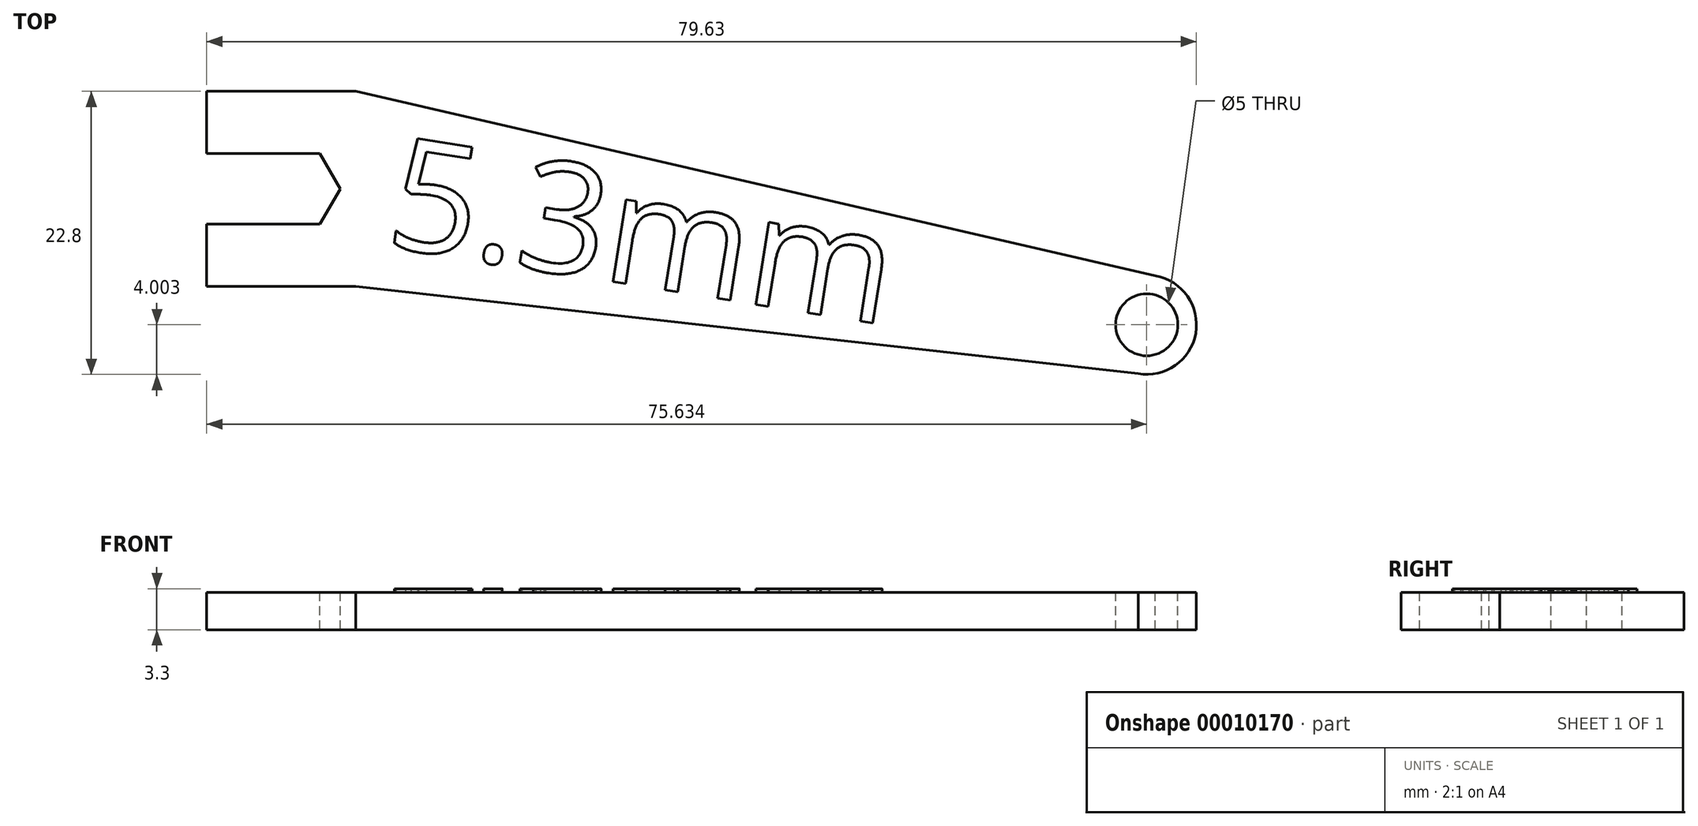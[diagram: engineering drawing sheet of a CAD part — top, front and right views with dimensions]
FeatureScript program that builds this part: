
annotation { "Feature Type Name" : "Feature", "Feature Type Description" : "" }
export const myFeature = defineFeature(function(context is Context, id is Id, definition is map)
    precondition{}
    {
        {
            var Q0;
            Q0=qCreatedBy(makeId("Top.planeOp"),FACE);
            var sketch = newSketch(context, id + "F0", { "sketchPlane" : qUnion([Q0])});
            skCircle(sketch, "E0.cCircle", {"center": v(-19.18, 8.62) * mm, "radius": 2.85 * mm, "construction": true});
            skLineSegment(sketch, "E0.0", {"start": v(-15.89, 8.62) * mm, "end": v(-17.53, 5.77) * mm});
            skLineSegment(sketch, "E0.1", {"start": v(-17.53, 5.77) * mm, "end": v(-20.82, 5.77) * mm});
            skLineSegment(sketch, "E0.2", {"start": v(-20.82, 5.77) * mm, "end": v(-22.47, 8.62) * mm, "construction": true});
            skLineSegment(sketch, "E0.3", {"start": v(-22.47, 8.62) * mm, "end": v(-20.82, 11.47) * mm, "construction": true});
            skLineSegment(sketch, "E0.4", {"start": v(-20.82, 11.47) * mm, "end": v(-17.53, 11.47) * mm});
            skLineSegment(sketch, "E0.5", {"start": v(-17.53, 11.47) * mm, "end": v(-15.89, 8.62) * mm});
            skPoint(sketch, "E0.0.midPoint", {"position": v(-16.7, 7.2) * mm});
            skCircle(sketch, "E1.cCircle", {"center": v(-19.18, 8.62) * mm, "radius": 7.85 * mm, "construction": true});
            skLineSegment(sketch, "E1.0", {"start": v(-14.64, 16.47) * mm, "end": v(-10.11, 8.62) * mm, "construction": true});
            skLineSegment(sketch, "E1.1", {"start": v(-10.11, 8.62) * mm, "end": v(-14.64, 0.77) * mm, "construction": true});
            skLineSegment(sketch, "E1.2", {"start": v(-14.64, 0.77) * mm, "end": v(-23.54, 0.77) * mm});
            skLineSegment(sketch, "E1.3", {"start": v(-23.54, 0.77) * mm, "end": v(-26.65, 5.77) * mm, "construction": true});
            skLineSegment(sketch, "E1.4", {"start": v(-26.65, 11.47) * mm, "end": v(-23.54, 16.47) * mm, "construction": true});
            skLineSegment(sketch, "E1.5", {"start": v(-23.54, 16.47) * mm, "end": v(-14.64, 16.47) * mm});
            skPoint(sketch, "E1.0.midPoint", {"position": v(-12.38, 12.54) * mm});
            skLineSegment(sketch, "E2", {"start": v(-26.65, 11.47) * mm, "end": v(-20.82, 11.47) * mm});
            skLineSegment(sketch, "E3", {"start": v(-26.65, 5.77) * mm, "end": v(-20.82, 5.77) * mm});
            skLineSegment(sketch, "E4", {"start": v(-23.54, 16.47) * mm, "end": v(-26.65, 16.47) * mm});
            skLineSegment(sketch, "E5", {"start": v(-26.65, 16.47) * mm, "end": v(-26.65, 11.47) * mm});
            skLineSegment(sketch, "E6", {"start": v(-26.65, 5.77) * mm, "end": v(-26.65, 0.77) * mm});
            skLineSegment(sketch, "E7", {"start": v(-26.65, 0.77) * mm, "end": v(-23.54, 0.77) * mm});
            skLineSegment(sketch, "E8", {"start": v(-19.18, 8.62) * mm, "end": v(-17.53, 11.47) * mm, "construction": true});
            skLineSegment(sketch, "E9.right", {"start": v(49.68, 1.61) * mm, "end": v(48.29, -6.27) * mm, "construction": true});
            skArc(sketch, "E10", {"start": v(48.29, -6.27) * mm, "mid": v(52.92, -3.02) * mm, "end": v(49.68, 1.61) * mm});
            skCircle(sketch, "E11", {"center": v(48.98, -2.33) * mm, "radius": 2.5 * mm});
            skLineSegment(sketch, "E12", {"start": v(-14.64, 16.47) * mm, "end": v(49.68, 1.61) * mm});
            skLineSegment(sketch, "E13", {"start": v(48.29, -6.27) * mm, "end": v(-14.64, 0.77) * mm});
            skSolve(sketch);
        }
        {
            var Q0;
            Q0=makeQuery(id+"F0.imprint","IMPRINT",FACE,{"disambiguationData":[TD([[makeQuery(id+"F0.imprint","IMPRINT",EDGE,{"derivedFrom":sQuery(id+"F0.wireOp",EDGE,"E0.0")}),1.0]])]});
            extrude(context, id + "F1", {"entities" : qUnion([Q0]), "oppositeDirection" : true, "depth" : 3 * mm});
        }
        {
            var Q0;
            Q0=qCreatedBy(makeId("Top.planeOp"),FACE);
            var sketch = newSketch(context, id + "F2", { "sketchPlane" : qUnion([Q0])});
            skText(sketch, "E14", { "text": "5.3mm", "fontName": "OpenSans-Regular.ttf"});
            const initialGuessF2  = {"E14": [-0.01242, 0.00406, 0.98768, -0.1565, 0.009]};
            skSetInitialGuess(sketch, initialGuessF2);
            skSolve(sketch);
        }
        {
            var Q0;
            Q0 = qSketchRegion(id + "F2", true);
            extrude(context, id + "F3", {"entities" : qUnion([Q0]), "operationType" : NewBodyOperationType.ADD, "depth" : 0.3 * mm});
        }
    });
